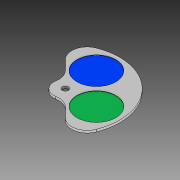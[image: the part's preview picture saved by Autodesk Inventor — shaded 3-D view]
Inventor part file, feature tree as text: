
AUTODESK INVENTOR PART (.ipt)
format: ipt  version: 2017 (Build 210142000, 142)  size: 155,136 bytes
history: native  units: mm
features: sketch x2, extrude x1, fillet x1, revolve x1, pattern_circular x1, projected_geometry x1
ambient origin geometry x8: Origin, YZ Plane, XZ Plane, XY Plane, X Axis, Y Axis, Z Axis, Center Point
bodies: Solid1 (feature_tree)
feature tree (7):
  extrude  "Extrusion1"  Depth=50.0mm
  fillet  "Fillet1"  Radius=30.0mm
  revolve  "Revolution1"  [1 undecoded]
  pattern_circular  "Circular Pattern1"  [2 undecoded]
  sketch  "Sketch1"  dims[d0=50.0mm d1=50.0mm d2=30.0mm]
  sketch  "Sketch2"  dims[d3=45.0deg d4=80.0mm d5=8.0mm d6=30.0mm d7=3.0mm d8=0.0mm d9=20.0mm d10=2.0mm d11=90.0deg d12=20.0mm d13=90.0deg]
  projected_geometry  "Projected Loop1"
note: 3 required parameter values undecoded (feature->parameter linkage not recoverable at this tier; creation-order binding heuristic only, values carry confidence <= 0.55)